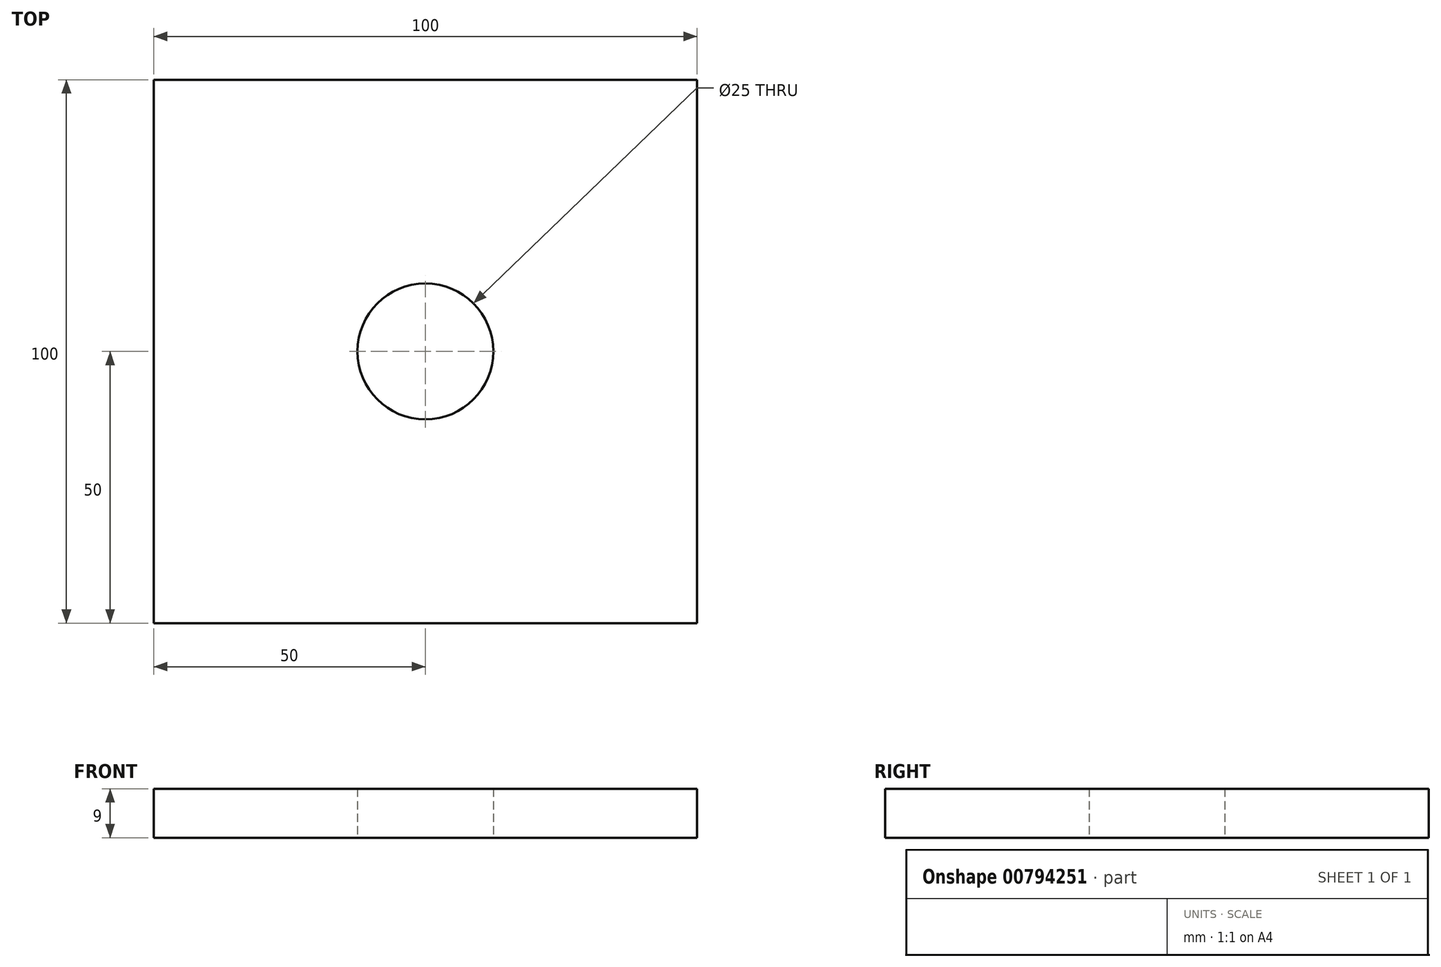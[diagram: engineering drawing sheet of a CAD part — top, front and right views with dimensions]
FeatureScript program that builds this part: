
annotation { "Feature Type Name" : "Feature", "Feature Type Description" : "" }
export const myFeature = defineFeature(function(context is Context, id is Id, definition is map)
    precondition{}
    {
        {
            var Q0;
            Q0=qCreatedBy(makeId("Top.planeOp"),FACE);
            var sketch = newSketch(context, id + "F0", { "sketchPlane" : qUnion([Q0])});
            skLineSegment(sketch, "E0.bottom", {"start": v(50, 50) * mm, "end": v(-50, 50) * mm});
            skLineSegment(sketch, "E0.top", {"start": v(50, -50) * mm, "end": v(-50, -50) * mm});
            skLineSegment(sketch, "E0.left", {"start": v(50, 50) * mm, "end": v(50, -50) * mm});
            skLineSegment(sketch, "E0.right", {"start": v(-50, 50) * mm, "end": v(-50, -50) * mm});
            skPoint(sketch, "E0.middle", {"position": v(0, 0) * mm});
            skCircle(sketch, "E1", {"center": v(0, 0) * mm, "radius": 12.5 * mm});
            skSolve(sketch);
        }
        {
            var Q0;
            Q0=makeQuery(id+"F0.imprint","IMPRINT",FACE,{"disambiguationData":[TD([[makeQuery(id+"F0.imprint","IMPRINT",EDGE,{"derivedFrom":sQuery(id+"F0.wireOp",EDGE,"E0.bottom")}),1.0]])]});
            var Q1;
            Q1 = qSketchRegion(id + "FCfHCbPlu1jVmf1_0", true);
            extrude(context, id + "F1", {"entities" : qUnion([Q0, Q1]), "depth" : 9 * mm, "offsetDistance" : 25 * mm});
        }
    });
